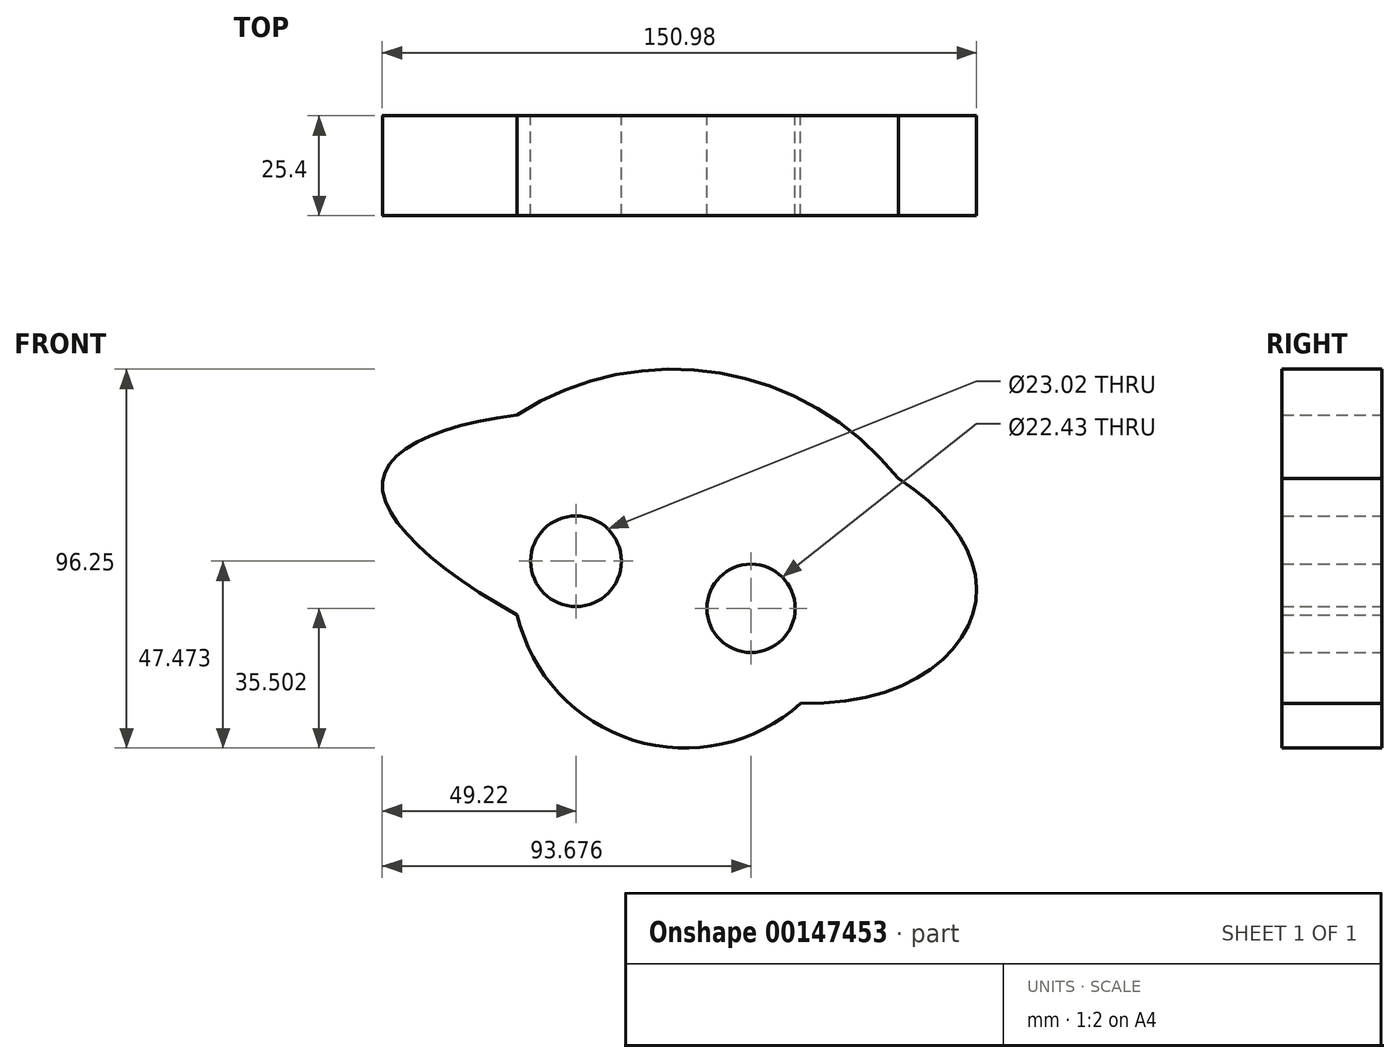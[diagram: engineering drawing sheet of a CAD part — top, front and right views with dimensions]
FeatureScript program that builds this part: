
annotation { "Feature Type Name" : "Feature", "Feature Type Description" : "" }
export const myFeature = defineFeature(function(context is Context, id is Id, definition is map)
    precondition{}
    {
        {
            var Q0;
            Q0=qCreatedBy(makeId("Front.planeOp"),FACE);
            var sketch = newSketch(context, id + "F0", { "sketchPlane" : qUnion([Q0])});
            skCircle(sketch, "E0", {"center": v(0, 0) * mm, "radius": 43.76 * mm});
            skFitSpline(sketch, "E1", {"points": [v(29.4, -32.41) * mm, v(74.07, -4.08) * mm, v(22.19, 37.72) * mm, v(-76.87, 23.7) * mm, v(29.4, -32.41) * mm]});
            skArc(sketch, "E2", {"start": v(54.18, 24.73) * mm, "mid": v(8.84, 51.5) * mm, "end": v(-42.72, 40.87) * mm});
            skCircle(sketch, "E3", {"center": v(-27.68, 3.71) * mm, "radius": 11.51 * mm});
            skCircle(sketch, "E4", {"center": v(16.78, -8.26) * mm, "radius": 11.22 * mm});
            skSolve(sketch);
        }
        {
            var Q0;
            {var subQ0=sQuery(id+"F0.wireOp",EDGE,"E1");var subQ1=sQuery(id+"F0.wireOp",EDGE,"E0");var subQ2=makeQuery(id+"F0.imprint","INTERSECT",VERTEX,{"disambiguationData":[OD(0.0)],"derivedFrom":[subQ1,subQ0]});Q0=makeQuery(id+"F0.imprint","IMPRINT",FACE,{"disambiguationData":[TD([[makeQuery(id+"F0.imprint","IMPRINT",EDGE,{"disambiguationData":[TD([[subQ2,-1.0]])],"derivedFrom":subQ1}),1.0]])]});}
            var Q1;
            {var subQ0=sQuery(id+"F0.wireOp",EDGE,"E1");var subQ1=sQuery(id+"F0.wireOp",EDGE,"E0");var subQ2=makeQuery(id+"F0.imprint","INTERSECT",VERTEX,{"disambiguationData":[OD(2.0)],"derivedFrom":[subQ1,subQ0]});Q1=makeQuery(id+"F0.imprint","IMPRINT",FACE,{"disambiguationData":[TD([[makeQuery(id+"F0.imprint","IMPRINT",EDGE,{"disambiguationData":[TD([[subQ2,-1.0]])],"derivedFrom":subQ1}),1.0]])]});}
            var Q2;
            {var subQ0=sQuery(id+"F0.wireOp",EDGE,"E1");var subQ1=sQuery(id+"F0.wireOp",EDGE,"E0");var subQ2=makeQuery(id+"F0.imprint","INTERSECT",VERTEX,{"disambiguationData":[OD(1.0)],"derivedFrom":[subQ1,subQ0]});Q2=makeQuery(id+"F0.imprint","IMPRINT",FACE,{"disambiguationData":[TD([[makeQuery(id+"F0.imprint","IMPRINT",EDGE,{"disambiguationData":[TD([[subQ2,1.0]])],"derivedFrom":subQ1}),-1.0]])]});}
            var Q3;
            {var subQ0=sQuery(id+"F0.wireOp",EDGE,"E1");var subQ1=sQuery(id+"F0.wireOp",EDGE,"E0");var subQ2=makeQuery(id+"F0.imprint","INTERSECT",VERTEX,{"disambiguationData":[OD(0.0)],"derivedFrom":[subQ1,subQ0]});Q3=makeQuery(id+"F0.imprint","IMPRINT",FACE,{"disambiguationData":[TD([[makeQuery(id+"F0.imprint","IMPRINT",EDGE,{"disambiguationData":[TD([[subQ2,-1.0]])],"derivedFrom":subQ1}),-1.0]])]});}
            extrude(context, id + "F1", {"entities" : qUnion([Q0, Q1, Q2, Q3]), "depth" : 25.4 * mm});
        }
        {
            var Q0;
            Q0 = qSketchRegion(id + "F0", true);
            extrude(context, id + "F2", {"entities" : qUnion([Q0]), "operationType" : NewBodyOperationType.ADD, "depth" : 25.4 * mm});
        }
    });
